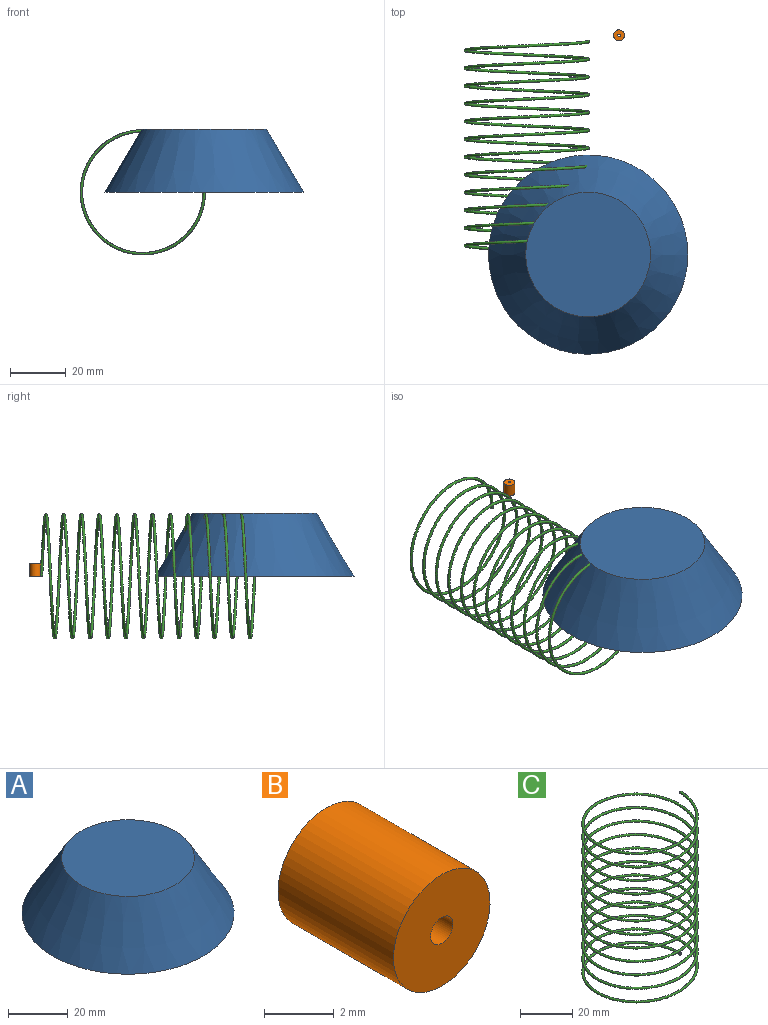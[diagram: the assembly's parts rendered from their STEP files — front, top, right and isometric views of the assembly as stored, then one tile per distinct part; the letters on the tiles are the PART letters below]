
ASSEMBLY  parts=3 mates=2
PART A: 3 faces, bbox 71.2x71.2x22.6 mm
  f0: plane 71.23x71.23mm, normal (0,0,-1), area 3985.4mm2, adj f2
  f1: plane 44.59x44.59mm, normal (0,0,1), area 1561.3mm2, adj f2
  f2: cone r=35.62mm half-angle=30.5deg, axis (0,0,-1), area 4774mm2, adj f0,f1
PART B: 4 faces, bbox 3.9x4.7x3.9 mm
  f0: cylinder r=0.46mm len=4.7mm, axis (0,-1,0), area 13.4mm2, adj f2,f3
  f1: cylinder r=1.96mm len=4.7mm, axis (0,-1,0), area 58mm2, adj f2,f3
  f2: plane 3.93x3.93mm, normal (0,1,0), area 11.5mm2, adj f0,f1
  f3: plane 3.93x3.93mm, normal (0,-1,0), area 11.5mm2, adj f0,f1
PART C: 3 faces, bbox 45.7x52.8x77.1 mm
  f0: plane 0.91x0.91mm, normal (0,1,0), area 0.7mm2, adj f2
  f1: plane 0.91x0.91mm, normal (0,-1,0), area 0.7mm2, adj f2
  f2: bspline ~77.11x52.78mm, area 4747mm2, adj f0,f1
PLACE A t=(0,0,15.75)mm fixed
PLACE B rot(axis=(-0.99,-0.1,0.1),90.6deg) t=(4.39,-0.62,96.9)mm
PLACE C rot(axis=(-1,0,0),90deg) t=(-21.94,0,92.2)mm
MATE pin_slot C.f0 <-> B.f0  axis (0,0,-1) through (0,76.2,92.2)mm
MATE cylindrical A.f2 <-> C.f1  axis (0,0,-1) through (0,0,92.2)mm
